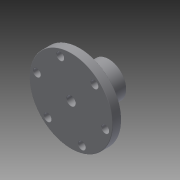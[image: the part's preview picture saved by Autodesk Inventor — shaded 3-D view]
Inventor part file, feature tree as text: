
AUTODESK INVENTOR PART (.ipt)
format: ipt  version: 2014 (Build 180170000, 170)  size: 207,872 bytes
history: native  units: mm
features: fillet x17, sketch x5, extrude x4, pattern_circular x1, plane x1, hole x1
ambient origin geometry x8: Origin, YZ Plane, XZ Plane, XY Plane, X Axis, Y Axis, Z Axis, Center Point
bodies: Volumenkörper1 (feature_tree)
feature tree (29):
  extrude  "Extrusion1"  Depth=6.0mm TaperAngle=0.0deg
  extrude  "Extrusion2"  Depth=48.0mm
  pattern_circular  "Runde Anordnung1"  Count=6 Angle=360.0deg
  extrude  "Extrusion3"  Depth=20.0mm TaperAngle=0.0deg
  extrude  "Extrusion4"  Depth=10.0mm TaperAngle=0.0deg
  fillet  "Rundung1"  Radius=0.25mm
  fillet  "Rundung2"  Radius=0.25mm
  fillet  "Rundung3"  Radius=0.25mm
  fillet  "Rundung4"  Radius=0.25mm
  fillet  "Rundung5"  Radius=0.25mm
  fillet  "Rundung6"  Radius=0.25mm
  fillet  "Rundung7"  Radius=0.25mm
  fillet  "Rundung8"  Radius=0.25mm
  fillet  "Rundung9"  Radius=0.25mm
  fillet  "Rundung10"  Radius=0.25mm
  fillet  "Rundung11"  Radius=0.25mm
  fillet  "Rundung12"  Radius=0.25mm
  fillet  "Rundung13"  Radius=0.25mm
  fillet  "Rundung14"  Radius=0.25mm
  fillet  "Rundung15"  Radius=0.25mm
  fillet  "Rundung16"  Radius=0.25mm
  fillet  "Rundung17"  Radius=0.25mm
  plane  "Arbeitsebene1"
  hole  "Bohrung1"  [1 undecoded]
  sketch  "Skizze1"  dims[d0=57.0mm d1=6.0mm d2=0.0mm]
  sketch  "Skizze2"  dims[d3=5.0mm d4=48.0mm]
  sketch  "Skizze3"  dims[d5=6.0mm d6=0.0mm d7=60.0mm d8=360.0deg]
  sketch  "Skizze4"  dims[d10=24.0mm d11=20.0mm d12=0.0mm]
  sketch  "Skizze7"  dims[d13=6.0mm d14=23.0mm d15=0.0mm d16=0.25mm d17=0.25mm d18=0.25mm d19=0.25mm d20=0.25mm d21=0.25mm d22=0.25mm d23=0.25mm d24=0.25mm d25=0.25mm d26=0.25mm d27=0.25mm d28=0.25mm d29=0.25mm d30=0.25mm d31=0.25mm d32=0.25mm d33=12.0mm d35=10.0mm d36=4.134mm d37=6.0mm d38=4.0mm d39=2.0mm d40=90.0deg d41=8.0mm d42=20.594885mm]
note: 1 required parameter value undecoded (feature->parameter linkage not recoverable at this tier; creation-order binding heuristic only, values carry confidence <= 0.55)
